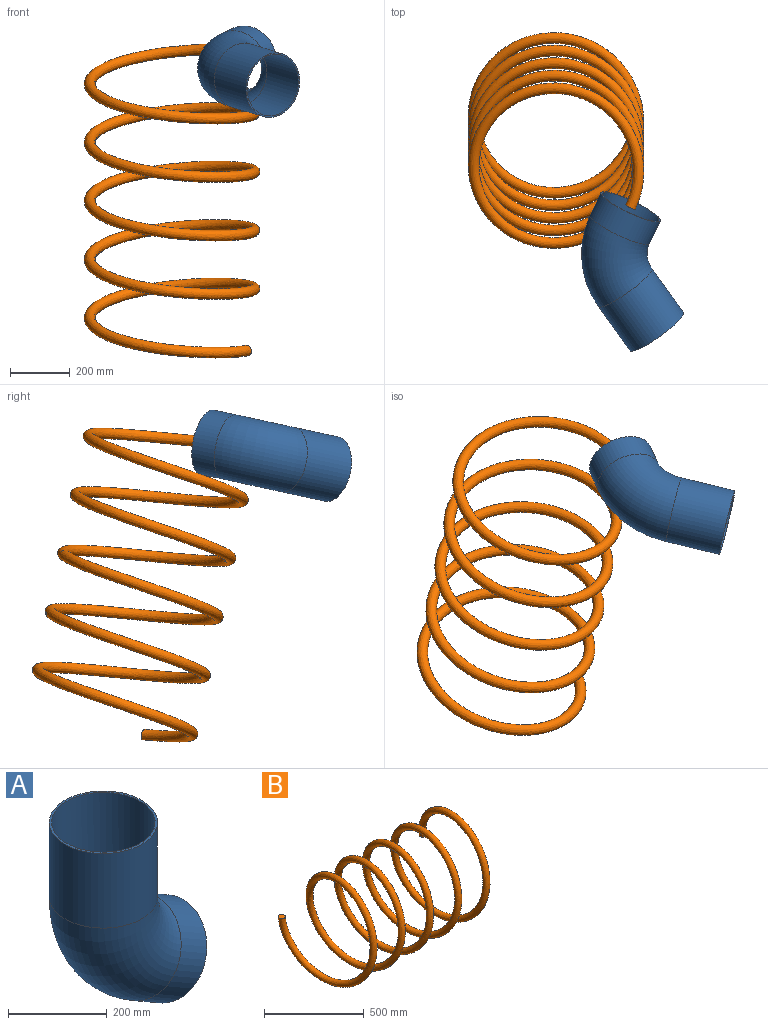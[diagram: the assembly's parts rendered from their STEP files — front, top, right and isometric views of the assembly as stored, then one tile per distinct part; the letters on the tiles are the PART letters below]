
ASSEMBLY  parts=2 mates=1
PART A: 8 faces, bbox 363x219x494.8 mm
  f0: plane 219x219mm, normal (0,0,1), area 3361.5mm2, adj f2,f5
  f1: plane 219x189.66mm, normal (0.87,0,-0.5), area 3361.5mm2, adj f4,f7
  f2: cylinder r=109.5mm len=219mm, axis (0,0,-1), area 126958.2mm2, adj f0,f3
  f3: torus R=200mm, axis (0,-1,0), area 144096.2mm2, adj f2,f4
  f4: cylinder r=109.5mm len=231.92mm, axis (0.87,0,-0.5), area 58157.3mm2, adj f1,f3
  f5: cylinder r=104.5mm len=209mm, axis (0,0,-1), area 121161mm2, adj f0,f6
  f6: torus R=200mm, axis (0,-1,0), area 137516.5mm2, adj f5,f7
  f7: cylinder r=104.5mm len=223.26mm, axis (0.87,0,-0.5), area 55501.8mm2, adj f1,f6
PART B: 3 faces, bbox 1036x622.1x622.1 mm
  f0: plane 36.04x36.04mm, normal (0,0,1), area 1020.1mm2, adj f2
  f1: plane 36.04x36.04mm, normal (0,0,-1), area 1020.1mm2, adj f2
  f2: bspline ~1036.04x622.08mm, area 981218.5mm2, adj f0,f1
PLACE A rot(axis=(0.93,0.24,0.29),106.4deg) t=(41.33,-273.25,33.75)mm
PLACE B rot(axis=(-0.62,-0.35,-0.71),127.6deg) t=(-295.45,469.41,-828.56)mm
MATE fastened B.f1 <-> A.f4  axis (-0.42,-0.89,-0.19) through (-46.21,144.08,124.16)mm
